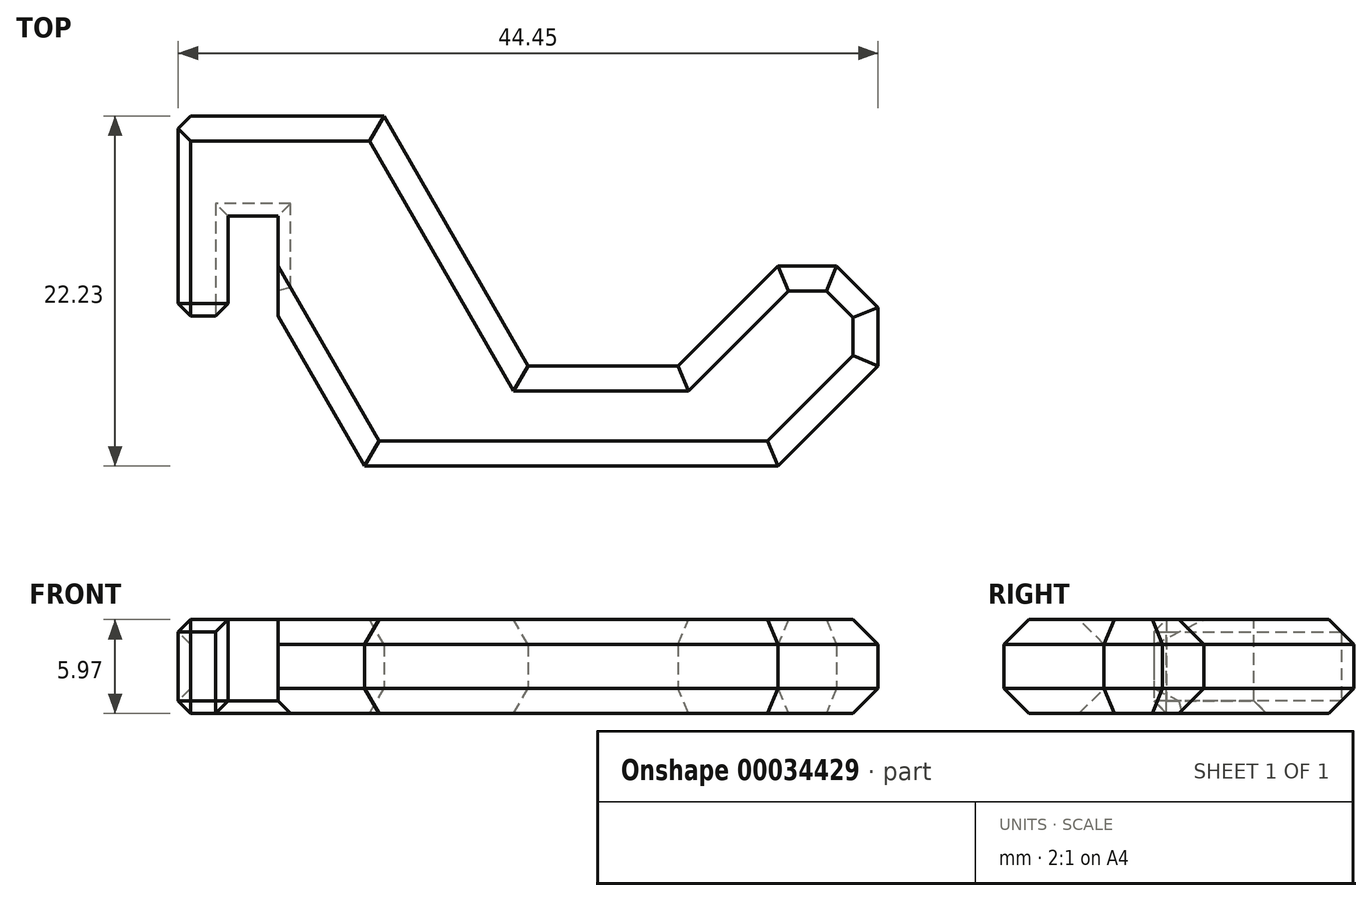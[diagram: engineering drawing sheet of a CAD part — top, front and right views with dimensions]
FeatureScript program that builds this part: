
annotation { "Feature Type Name" : "Feature", "Feature Type Description" : "" }
export const myFeature = defineFeature(function(context is Context, id is Id, definition is map)
    precondition{}
    {
        {
            var Q0;
            Q0=qCreatedBy(makeId("Top.planeOp"),FACE);
            var sketch = newSketch(context, id + "F0", { "sketchPlane" : qUnion([Q0])});
            skLineSegment(sketch, "E0", {"start": v(0, 0) * mm, "end": v(0, -12.7) * mm});
            skLineSegment(sketch, "E1", {"start": v(0, -12.7) * mm, "end": v(6.35, -12.7) * mm});
            skLineSegment(sketch, "E2", {"start": v(6.35, -12.7) * mm, "end": v(11.85, -22.22) * mm});
            skLineSegment(sketch, "E3", {"start": v(11.85, -22.23) * mm, "end": v(38.1, -22.23) * mm});
            skLineSegment(sketch, "E4", {"start": v(38.1, -22.23) * mm, "end": v(44.45, -15.88) * mm});
            skLineSegment(sketch, "E5", {"start": v(44.45, -15.88) * mm, "end": v(44.45, -12.16) * mm});
            skLineSegment(sketch, "E6", {"start": v(38.1, -9.52) * mm, "end": v(31.75, -15.88) * mm});
            skLineSegment(sketch, "E7", {"start": v(31.75, -15.88) * mm, "end": v(22.23, -15.88) * mm});
            skLineSegment(sketch, "E8", {"start": v(22.23, -15.88) * mm, "end": v(13.06, 0) * mm});
            skLineSegment(sketch, "E9", {"start": v(13.06, 0) * mm, "end": v(0, 0) * mm});
            skLineSegment(sketch, "E10", {"start": v(38.1, -9.52) * mm, "end": v(41.82, -9.52) * mm});
            skLineSegment(sketch, "E11", {"start": v(41.82, -9.53) * mm, "end": v(44.45, -12.16) * mm});
            skSolve(sketch);
        }
        {
            var Q0;
            Q0 = qSketchRegion(id + "F0", true);
            extrude(context, id + "F1", {"entities" : qUnion([Q0]), "depth" : 5.97 * mm});
        }
        {
            var Q0;
            Q0=makeQuery(id+"F1.opExtrude","CAP_FACE",FACE,{"disambiguationData":[OSD([sQuery(id+"F0.wireOp",EDGE,"E0"),sQuery(id+"F0.wireOp",EDGE,"E1"),sQuery(id+"F0.wireOp",EDGE,"E2"),sQuery(id+"F0.wireOp",EDGE,"E3"),sQuery(id+"F0.wireOp",EDGE,"E4"),sQuery(id+"F0.wireOp",EDGE,"E5"),sQuery(id+"F0.wireOp",EDGE,"E6"),sQuery(id+"F0.wireOp",EDGE,"E7"),sQuery(id+"F0.wireOp",EDGE,"E8"),sQuery(id+"F0.wireOp",EDGE,"E9"),sQuery(id+"F0.wireOp",EDGE,"E10"),sQuery(id+"F0.wireOp",EDGE,"E11")])],"isStart":false});
            var sketch = newSketch(context, id + "F2", { "sketchPlane" : qUnion([Q0])});
            skLineSegment(sketch, "E12.bottom", {"start": v(6.35, -12.7) * mm, "end": v(3.18, -12.7) * mm});
            skLineSegment(sketch, "E12.top", {"start": v(6.35, -6.35) * mm, "end": v(3.17, -6.35) * mm});
            skLineSegment(sketch, "E12.left", {"start": v(6.35, -12.7) * mm, "end": v(6.35, -6.35) * mm});
            skLineSegment(sketch, "E12.right", {"start": v(3.18, -12.7) * mm, "end": v(3.18, -6.35) * mm});
            skSolve(sketch);
        }
        {
            var Q0;
            Q0 = qSketchRegion(id + "F2", true);
            extrude(context, id + "F3", {"entities" : qUnion([Q0]), "operationType" : NewBodyOperationType.REMOVE, "endBound" : BoundingType.THROUGH_ALL, "oppositeDirection" : true, "depth" : 25.4 * mm});
        }
        {
            var Q0;
            Q0=makeQuery(id+"F1.opExtrude","SWEPT_FACE",FACE,{"disambiguationData":[OSD([sQuery(id+"F0.wireOp",EDGE,"E0")])]});
            var Q1;
            Q1=makeQuery(id+"F1.opExtrude","SWEPT_FACE",FACE,{"disambiguationData":[OSD([sQuery(id+"F0.wireOp",EDGE,"E1")])]});
            var Q2;
            Q2=makeQuery(id+"F3.boolean.opBoolean","COPY",EDGE,{"derivedFrom":makeQuery(id+"F3.opExtrude","CAP_EDGE",EDGE,{"disambiguationData":[OSD([sQuery(id+"F2.wireOp",EDGE,"E12.right")])],"isStart":true})});
            var Q3;
            Q3=makeQuery(id+"F3.boolean.opBoolean","INTERSECT",EDGE,{"derivedFrom":[makeQuery(id+"F1.opExtrude","CAP_FACE",FACE,{"disambiguationData":[OSD([sQuery(id+"F0.wireOp",EDGE,"E0"),sQuery(id+"F0.wireOp",EDGE,"E1"),sQuery(id+"F0.wireOp",EDGE,"E2"),sQuery(id+"F0.wireOp",EDGE,"E3"),sQuery(id+"F0.wireOp",EDGE,"E4"),sQuery(id+"F0.wireOp",EDGE,"E5"),sQuery(id+"F0.wireOp",EDGE,"E6"),sQuery(id+"F0.wireOp",EDGE,"E7"),sQuery(id+"F0.wireOp",EDGE,"E8"),sQuery(id+"F0.wireOp",EDGE,"E9"),sQuery(id+"F0.wireOp",EDGE,"E10"),sQuery(id+"F0.wireOp",EDGE,"E11")])],"isStart":true}),makeQuery(id+"F3.opExtrude","SWEPT_FACE",FACE,{"disambiguationData":[OSD([sQuery(id+"F2.wireOp",EDGE,"E12.right")])]})]});
            var Q4;
            Q4=makeQuery(id+"F3.boolean.opBoolean","COPY",EDGE,{"derivedFrom":makeQuery(id+"F3.opExtrude","CAP_EDGE",EDGE,{"disambiguationData":[OSD([sQuery(id+"F2.wireOp",EDGE,"E12.top")])],"isStart":true})});
            var Q5;
            Q5=makeQuery(id+"F3.boolean.opBoolean","COPY",EDGE,{"derivedFrom":makeQuery(id+"F3.opExtrude","CAP_EDGE",EDGE,{"disambiguationData":[OSD([sQuery(id+"F2.wireOp",EDGE,"E12.left")])],"isStart":true})});
            var Q6;
            Q6=makeQuery(id+"F3.boolean.opBoolean","INTERSECT",EDGE,{"derivedFrom":[makeQuery(id+"F1.opExtrude","CAP_FACE",FACE,{"disambiguationData":[OSD([sQuery(id+"F0.wireOp",EDGE,"E0"),sQuery(id+"F0.wireOp",EDGE,"E1"),sQuery(id+"F0.wireOp",EDGE,"E2"),sQuery(id+"F0.wireOp",EDGE,"E3"),sQuery(id+"F0.wireOp",EDGE,"E4"),sQuery(id+"F0.wireOp",EDGE,"E5"),sQuery(id+"F0.wireOp",EDGE,"E6"),sQuery(id+"F0.wireOp",EDGE,"E7"),sQuery(id+"F0.wireOp",EDGE,"E8"),sQuery(id+"F0.wireOp",EDGE,"E9"),sQuery(id+"F0.wireOp",EDGE,"E10"),sQuery(id+"F0.wireOp",EDGE,"E11")])],"isStart":true}),makeQuery(id+"F3.opExtrude","SWEPT_FACE",FACE,{"disambiguationData":[OSD([sQuery(id+"F2.wireOp",EDGE,"E12.top")])]})]});
            var Q7;
            Q7=makeQuery(id+"F3.boolean.opBoolean","INTERSECT",EDGE,{"derivedFrom":[makeQuery(id+"F1.opExtrude","CAP_FACE",FACE,{"disambiguationData":[OSD([sQuery(id+"F0.wireOp",EDGE,"E0"),sQuery(id+"F0.wireOp",EDGE,"E1"),sQuery(id+"F0.wireOp",EDGE,"E2"),sQuery(id+"F0.wireOp",EDGE,"E3"),sQuery(id+"F0.wireOp",EDGE,"E4"),sQuery(id+"F0.wireOp",EDGE,"E5"),sQuery(id+"F0.wireOp",EDGE,"E6"),sQuery(id+"F0.wireOp",EDGE,"E7"),sQuery(id+"F0.wireOp",EDGE,"E8"),sQuery(id+"F0.wireOp",EDGE,"E9"),sQuery(id+"F0.wireOp",EDGE,"E10"),sQuery(id+"F0.wireOp",EDGE,"E11")])],"isStart":true}),makeQuery(id+"F3.opExtrude","SWEPT_FACE",FACE,{"disambiguationData":[OSD([sQuery(id+"F2.wireOp",EDGE,"E12.left")])]})]});
            chamfer(context, id + "F4", {"entities" : qUnion([Q0, Q1, Q2, Q3, Q4, Q5, Q6, Q7]), "width" : 0.8 * mm, "tangentPropagation" : true});
        }
        {
            var Q0;
            Q0=makeQuery(id+"F1.opExtrude","CAP_EDGE",EDGE,{"disambiguationData":[OSD([sQuery(id+"F0.wireOp",EDGE,"E9")])],"isStart":true});
            var Q1;
            Q1=makeQuery(id+"F1.opExtrude","CAP_EDGE",EDGE,{"disambiguationData":[OSD([sQuery(id+"F0.wireOp",EDGE,"E8")])],"isStart":true});
            var Q2;
            Q2=makeQuery(id+"F1.opExtrude","CAP_EDGE",EDGE,{"disambiguationData":[OSD([sQuery(id+"F0.wireOp",EDGE,"E7")])],"isStart":true});
            var Q3;
            Q3=makeQuery(id+"F1.opExtrude","CAP_EDGE",EDGE,{"disambiguationData":[OSD([sQuery(id+"F0.wireOp",EDGE,"E6")])],"isStart":true});
            var Q4;
            Q4=makeQuery(id+"F1.opExtrude","CAP_EDGE",EDGE,{"disambiguationData":[OSD([sQuery(id+"F0.wireOp",EDGE,"E10")])],"isStart":true});
            var Q5;
            Q5=makeQuery(id+"F1.opExtrude","CAP_EDGE",EDGE,{"disambiguationData":[OSD([sQuery(id+"F0.wireOp",EDGE,"E11")])],"isStart":true});
            var Q6;
            Q6=makeQuery(id+"F1.opExtrude","CAP_EDGE",EDGE,{"disambiguationData":[OSD([sQuery(id+"F0.wireOp",EDGE,"E5")])],"isStart":true});
            var Q7;
            Q7=makeQuery(id+"F1.opExtrude","CAP_EDGE",EDGE,{"disambiguationData":[OSD([sQuery(id+"F0.wireOp",EDGE,"E4")])],"isStart":true});
            var Q8;
            Q8=makeQuery(id+"F1.opExtrude","CAP_EDGE",EDGE,{"disambiguationData":[OSD([sQuery(id+"F0.wireOp",EDGE,"E3")])],"isStart":true});
            var Q9;
            Q9=makeQuery(id+"F1.opExtrude","CAP_EDGE",EDGE,{"disambiguationData":[OSD([sQuery(id+"F0.wireOp",EDGE,"E2")])],"isStart":true});
            var Q10;
            Q10=makeQuery(id+"F1.opExtrude","CAP_EDGE",EDGE,{"disambiguationData":[OSD([sQuery(id+"F0.wireOp",EDGE,"E2")])],"isStart":false});
            var Q11;
            Q11=makeQuery(id+"F1.opExtrude","CAP_EDGE",EDGE,{"disambiguationData":[OSD([sQuery(id+"F0.wireOp",EDGE,"E3")])],"isStart":false});
            var Q12;
            Q12=makeQuery(id+"F1.opExtrude","CAP_EDGE",EDGE,{"disambiguationData":[OSD([sQuery(id+"F0.wireOp",EDGE,"E4")])],"isStart":false});
            var Q13;
            Q13=makeQuery(id+"F1.opExtrude","CAP_EDGE",EDGE,{"disambiguationData":[OSD([sQuery(id+"F0.wireOp",EDGE,"E5")])],"isStart":false});
            var Q14;
            Q14=makeQuery(id+"F1.opExtrude","CAP_EDGE",EDGE,{"disambiguationData":[OSD([sQuery(id+"F0.wireOp",EDGE,"E11")])],"isStart":false});
            var Q15;
            Q15=makeQuery(id+"F1.opExtrude","CAP_EDGE",EDGE,{"disambiguationData":[OSD([sQuery(id+"F0.wireOp",EDGE,"E6")])],"isStart":false});
            var Q16;
            Q16=makeQuery(id+"F1.opExtrude","CAP_EDGE",EDGE,{"disambiguationData":[OSD([sQuery(id+"F0.wireOp",EDGE,"E10")])],"isStart":false});
            var Q17;
            Q17=makeQuery(id+"F1.opExtrude","CAP_EDGE",EDGE,{"disambiguationData":[OSD([sQuery(id+"F0.wireOp",EDGE,"E7")])],"isStart":false});
            var Q18;
            Q18=makeQuery(id+"F1.opExtrude","CAP_EDGE",EDGE,{"disambiguationData":[OSD([sQuery(id+"F0.wireOp",EDGE,"E8")])],"isStart":false});
            var Q19;
            Q19=makeQuery(id+"F1.opExtrude","CAP_EDGE",EDGE,{"disambiguationData":[OSD([sQuery(id+"F0.wireOp",EDGE,"E9")])],"isStart":false});
            chamfer(context, id + "F5", {"entities" : qUnion([Q0, Q1, Q2, Q3, Q4, Q5, Q6, Q7, Q8, Q9, Q10, Q11, Q12, Q13, Q14, Q15, Q16, Q17, Q18, Q19]), "width" : 1.59 * mm, "tangentPropagation" : true});
        }
    });
